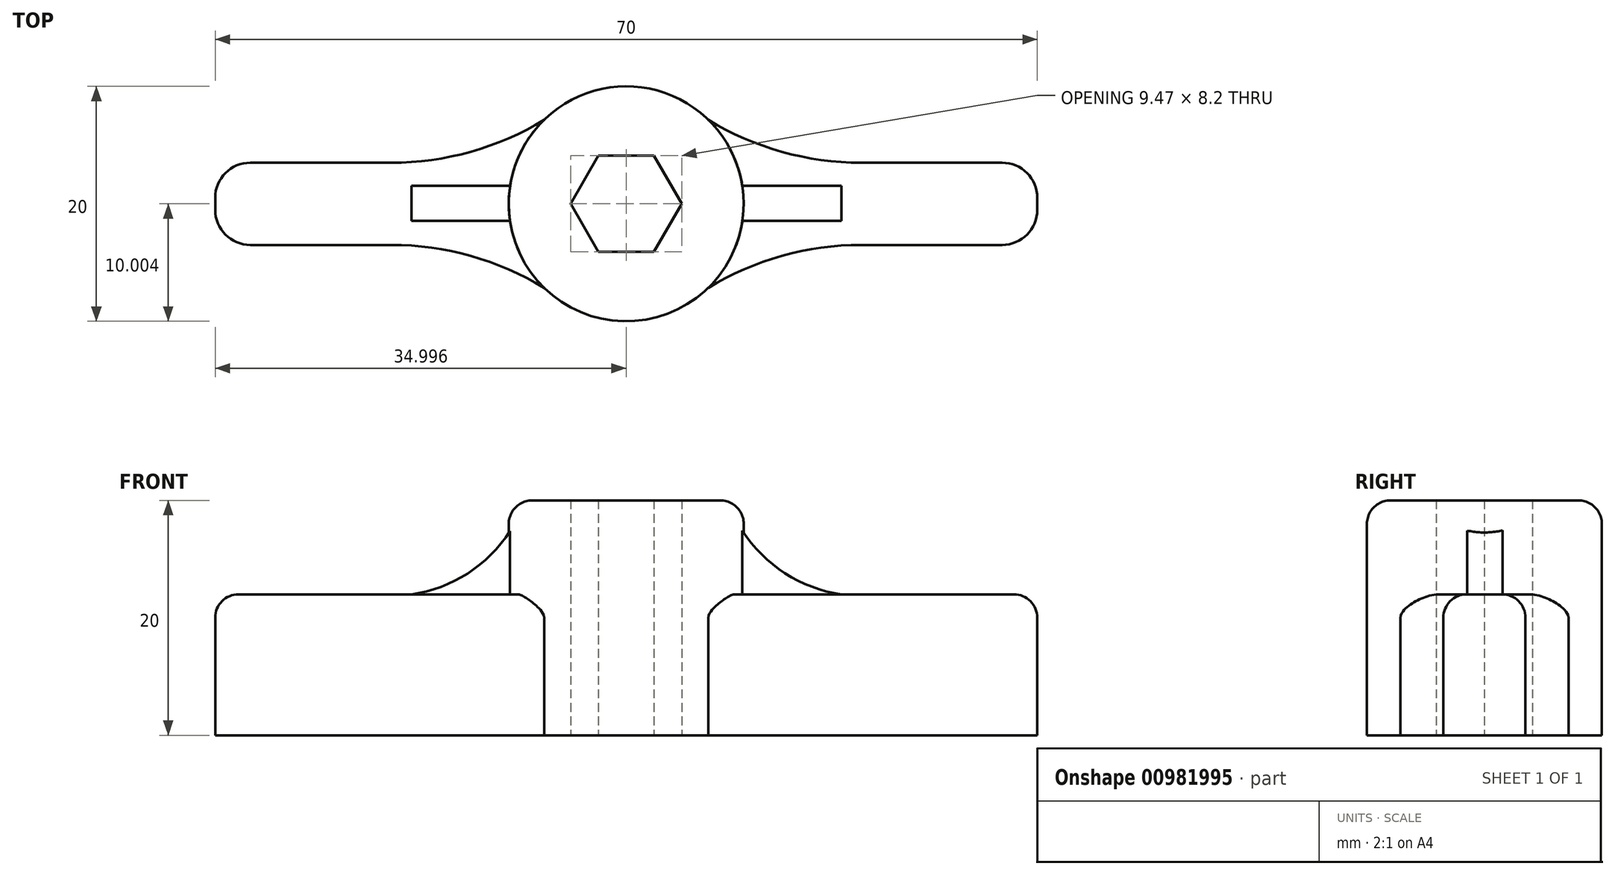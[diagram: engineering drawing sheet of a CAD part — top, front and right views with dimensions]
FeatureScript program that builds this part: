
annotation { "Feature Type Name" : "Feature", "Feature Type Description" : "" }
export const myFeature = defineFeature(function(context is Context, id is Id, definition is map)
    precondition{}
    {
        {
            var Q0;
            Q0=qCreatedBy(makeId("Top.planeOp"),FACE);
            var sketch = newSketch(context, id + "F0", { "sketchPlane" : qUnion([Q0])});
            skLineSegment(sketch, "E0.bottom", {"start": v(-35.01, 1.95) * mm, "end": v(34.99, 1.95) * mm});
            skLineSegment(sketch, "E0.top", {"start": v(-35.01, -5.05) * mm, "end": v(34.99, -5.05) * mm});
            skLineSegment(sketch, "E0.left", {"start": v(-35.01, 1.95) * mm, "end": v(-35.01, -5.05) * mm});
            skLineSegment(sketch, "E0.right", {"start": v(34.99, 1.95) * mm, "end": v(34.99, -5.05) * mm});
            skCircle(sketch, "E1", {"center": v(-0.01, -1.55) * mm, "radius": 10 * mm});
            skCircle(sketch, "E2.cCircle", {"center": v(-0.01, -1.55) * mm, "radius": 4.1 * mm, "construction": true});
            skLineSegment(sketch, "E2.0", {"start": v(-2.38, 2.55) * mm, "end": v(2.35, 2.55) * mm});
            skLineSegment(sketch, "E2.1", {"start": v(2.35, 2.55) * mm, "end": v(4.72, -1.55) * mm});
            skLineSegment(sketch, "E2.2", {"start": v(4.72, -1.55) * mm, "end": v(2.35, -5.65) * mm});
            skLineSegment(sketch, "E2.3", {"start": v(2.35, -5.65) * mm, "end": v(-2.38, -5.65) * mm});
            skLineSegment(sketch, "E2.4", {"start": v(-2.38, -5.65) * mm, "end": v(-4.75, -1.55) * mm});
            skLineSegment(sketch, "E2.5", {"start": v(-4.75, -1.55) * mm, "end": v(-2.38, 2.55) * mm});
            skPoint(sketch, "E2.0.midPoint", {"position": v(-0.01, 2.55) * mm});
            skLineSegment(sketch, "E3.bottom", {"start": v(-7, 5.6) * mm, "end": v(6.97, 5.6) * mm, "construction": true});
            skLineSegment(sketch, "E3.top", {"start": v(-7, -8.7) * mm, "end": v(6.97, -8.7) * mm, "construction": true});
            skLineSegment(sketch, "E4.top", {"start": v(-0.01, 1.95) * mm, "end": v(19.99, 1.95) * mm, "construction": true});
            skLineSegment(sketch, "E5.top", {"start": v(-0.01, -5.05) * mm, "end": v(19.99, -5.05) * mm, "construction": true});
            skLineSegment(sketch, "E6.top", {"start": v(-0.01, 1.95) * mm, "end": v(-20.01, 1.95) * mm, "construction": true});
            skLineSegment(sketch, "E7.top", {"start": v(-0.01, -5.05) * mm, "end": v(-20.01, -5.05) * mm, "construction": true});
            skArc(sketch, "E8", {"start": v(-20.01, 1.95) * mm, "mid": v(-13.26, 2.88) * mm, "end": v(-7, 5.6) * mm});
            skArc(sketch, "E9", {"start": v(-7, -8.7) * mm, "mid": v(-13.26, -5.98) * mm, "end": v(-20.01, -5.05) * mm});
            skArc(sketch, "E10", {"start": v(6.97, 5.6) * mm, "mid": v(13.23, 2.88) * mm, "end": v(19.99, 1.95) * mm});
            skArc(sketch, "E11", {"start": v(19.99, -5.05) * mm, "mid": v(13.23, -5.98) * mm, "end": v(6.97, -8.7) * mm});
            skSolve(sketch);
        }
        {
            var Q0;
            {var subQ10=sQuery(id+"F0.wireOp",EDGE,"E2.3");Q0=makeQuery(id+"F0.imprint","IMPRINT",FACE,{"disambiguationData":[TD([[makeQuery(id+"F0.imprint","IMPRINT",EDGE,{"derivedFrom":subQ10}),1.0]])]});}
            var Q1;
            {var subQ5=sQuery(id+"F0.wireOp",EDGE,"E1");var subQ7=sQuery(id+"F0.wireOp",EDGE,"E0.bottom");var subQ8=makeQuery(id+"F0.imprint","INTERSECT",VERTEX,{"disambiguationData":[OD(0.0)],"derivedFrom":[subQ7,subQ5]});Q1=makeQuery(id+"F0.imprint","IMPRINT",FACE,{"disambiguationData":[TD([[makeQuery(id+"F0.imprint","IMPRINT",EDGE,{"disambiguationData":[TD([[subQ8,-1.0]])],"derivedFrom":subQ7}),-1.0]])]});}
            var Q2;
            {var subQ10=sQuery(id+"F0.wireOp",EDGE,"E2.0");Q2=makeQuery(id+"F0.imprint","IMPRINT",FACE,{"disambiguationData":[TD([[makeQuery(id+"F0.imprint","IMPRINT",EDGE,{"derivedFrom":subQ10}),1.0]])]});}
            var Q3;
            {var subQ1=sQuery(id+"F0.wireOp",EDGE,"E0.bottom");var subQ6=sQuery(id+"F0.wireOp",EDGE,"E2.1");var subQ8=makeQuery(id+"F0.imprint","INTERSECT",VERTEX,{"derivedFrom":[subQ1,subQ6]});Q3=makeQuery(id+"F0.imprint","IMPRINT",FACE,{"disambiguationData":[TD([[makeQuery(id+"F0.imprint","IMPRINT",EDGE,{"disambiguationData":[TD([[subQ8,-1.0]])],"derivedFrom":subQ1}),-1.0]])]});}
            extrude(context, id + "F1", {"entities" : qUnion([Q0, Q1, Q2, Q3]), "depth" : 20 * mm, "offsetDistance" : 25 * mm});
        }
        {
            var Q0;
            {var subQ0=sQuery(id+"F0.wireOp",EDGE,"E11");Q0=makeQuery(id+"F0.imprint","IMPRINT",FACE,{"disambiguationData":[TD([[makeQuery(id+"F0.imprint","IMPRINT",EDGE,{"derivedFrom":subQ0}),-1.0]])]});}
            var Q1;
            {var subQ0=sQuery(id+"F0.wireOp",EDGE,"E10");Q1=makeQuery(id+"F0.imprint","IMPRINT",FACE,{"disambiguationData":[TD([[makeQuery(id+"F0.imprint","IMPRINT",EDGE,{"derivedFrom":subQ0}),-1.0]])]});}
            var Q2;
            {var subQ0=sQuery(id+"F0.wireOp",EDGE,"E0.right");Q2=makeQuery(id+"F0.imprint","IMPRINT",FACE,{"disambiguationData":[TD([[makeQuery(id+"F0.imprint","IMPRINT",EDGE,{"derivedFrom":subQ0}),-1.0]])]});}
            var Q3;
            {var subQ0=sQuery(id+"F0.wireOp",EDGE,"E9");Q3=makeQuery(id+"F0.imprint","IMPRINT",FACE,{"disambiguationData":[TD([[makeQuery(id+"F0.imprint","IMPRINT",EDGE,{"derivedFrom":subQ0}),-1.0]])]});}
            var Q4;
            {var subQ6=sQuery(id+"F0.wireOp",EDGE,"E0.left");Q4=makeQuery(id+"F0.imprint","IMPRINT",FACE,{"disambiguationData":[TD([[makeQuery(id+"F0.imprint","IMPRINT",EDGE,{"derivedFrom":subQ6}),1.0]])]});}
            var Q5;
            {var subQ0=sQuery(id+"F0.wireOp",EDGE,"E8");Q5=makeQuery(id+"F0.imprint","IMPRINT",FACE,{"disambiguationData":[TD([[makeQuery(id+"F0.imprint","IMPRINT",EDGE,{"derivedFrom":subQ0}),-1.0]])]});}
            extrude(context, id + "F2", {"entities" : qUnion([Q0, Q1, Q2, Q3, Q4, Q5]), "operationType" : NewBodyOperationType.ADD, "depth" : 12 * mm, "offsetDistance" : 25 * mm});
        }
        {
            var Q0;
            Q0=makeQuery(id+"F2.opExtrude","SWEPT_EDGE",EDGE,{"disambiguationData":[OSD([sQuery(id+"F0.wireOp",EDGE,"E0.bottom"),sQuery(id+"F0.wireOp",EDGE,"E0.left")])]});
            var Q1;
            Q1=makeQuery(id+"F2.opExtrude","SWEPT_EDGE",EDGE,{"disambiguationData":[OSD([sQuery(id+"F0.wireOp",EDGE,"E0.top"),sQuery(id+"F0.wireOp",EDGE,"E0.left")])]});
            var Q2;
            Q2=makeQuery(id+"F2.opExtrude","SWEPT_EDGE",EDGE,{"disambiguationData":[OSD([sQuery(id+"F0.wireOp",EDGE,"E0.top"),sQuery(id+"F0.wireOp",EDGE,"E0.right")])]});
            var Q3;
            Q3=makeQuery(id+"F2.opExtrude","SWEPT_EDGE",EDGE,{"disambiguationData":[OSD([sQuery(id+"F0.wireOp",EDGE,"E0.bottom"),sQuery(id+"F0.wireOp",EDGE,"E0.right")])]});
            fillet(context, id + "F3", {"entities" : qUnion([Q0, Q1, Q2, Q3]), "radius" : 3 * mm, "tangentPropagation" : true, "allowEdgeOverflow" : false});
        }
        {
            var Q0;
            {var subQ0=sQuery(id+"F0.wireOp",EDGE,"E0.top");Q0=makeQuery(id+"F2.opExtrude","CAP_EDGE",EDGE,{"disambiguationData":[OSD([subQ0]),TDD([makeQuery(id+"F0.imprint","IMPRINT",EDGE,{"disambiguationData":[TD([[makeQuery(id+"F0.imprint","INTERSECT",VERTEX,{"derivedFrom":[subQ0,sQuery(id+"F0.wireOp",EDGE,"E0.left")]}),-1.0]])],"derivedFrom":subQ0})])],"isStart":false});}
            var Q1;
            Q1=makeQuery(id+"F2.opExtrude","CAP_EDGE",EDGE,{"disambiguationData":[OSD([sQuery(id+"F0.wireOp",EDGE,"E11")])],"isStart":false});
            var Q2;
            Q2=makeQuery(id+"F1.opExtrude","CAP_EDGE",EDGE,{"disambiguationData":[OSD([sQuery(id+"F0.wireOp",EDGE,"E1")])],"isStart":false});
            fillet(context, id + "F4", {"entities" : qUnion([Q0, Q1, Q2]), "radius" : 2 * mm, "tangentPropagation" : true, "allowEdgeOverflow" : false});
        }
        {
            var Q0;
            Q0=qCreatedBy(makeId("Front.planeOp"),FACE);
            var sketch = newSketch(context, id + "F5", { "sketchPlane" : qUnion([Q0])});
            skArc(sketch, "E12", {"start": v(-20, 11.88) * mm, "mid": v(-13.96, 13.5) * mm, "end": v(-9.57, 17.95) * mm});
            skArc(sketch, "E13", {"start": v(9.57, 17.95) * mm, "mid": v(13.96, 13.5) * mm, "end": v(20, 11.88) * mm});
            skLineSegment(sketch, "E14", {"start": v(-20, 11.88) * mm, "end": v(-9.57, 11.88) * mm});
            skLineSegment(sketch, "E15", {"start": v(-9.57, 11.88) * mm, "end": v(-9.57, 17.95) * mm});
            skLineSegment(sketch, "E16", {"start": v(20, 11.88) * mm, "end": v(9.57, 11.88) * mm});
            skLineSegment(sketch, "E17", {"start": v(9.57, 11.88) * mm, "end": v(9.57, 17.95) * mm});
            skSolve(sketch);
        }
        {
            var Q0;
            Q0=makeQuery(id+"F5.imprint","IMPRINT",FACE,{"disambiguationData":[TD([[makeQuery(id+"F5.imprint","IMPRINT",EDGE,{"derivedFrom":sQuery(id+"F5.wireOp",EDGE,"E12")}),-1.0]])]});
            var Q1;
            Q1=makeQuery(id+"F5.imprint","IMPRINT",FACE,{"disambiguationData":[TD([[makeQuery(id+"F5.imprint","IMPRINT",EDGE,{"derivedFrom":sQuery(id+"F5.wireOp",EDGE,"E13")}),-1.0]])]});
            var Q2;
            Q2=sQuery(id+"F5.wireOp",EDGE,"E14");
            var Q3;
            Q3=sQuery(id+"F5.wireOp",EDGE,"E15");
            var Q4;
            Q4=sQuery(id+"F5.wireOp",EDGE,"E12");
            extrude(context, id + "F6", {"entities" : qUnion([Q0, Q1]), "operationType" : NewBodyOperationType.ADD, "surfaceEntities" : qUnion([Q2, Q3, Q4]), "depth" : 3 * mm, "offsetDistance" : 25 * mm});
        }
    });
